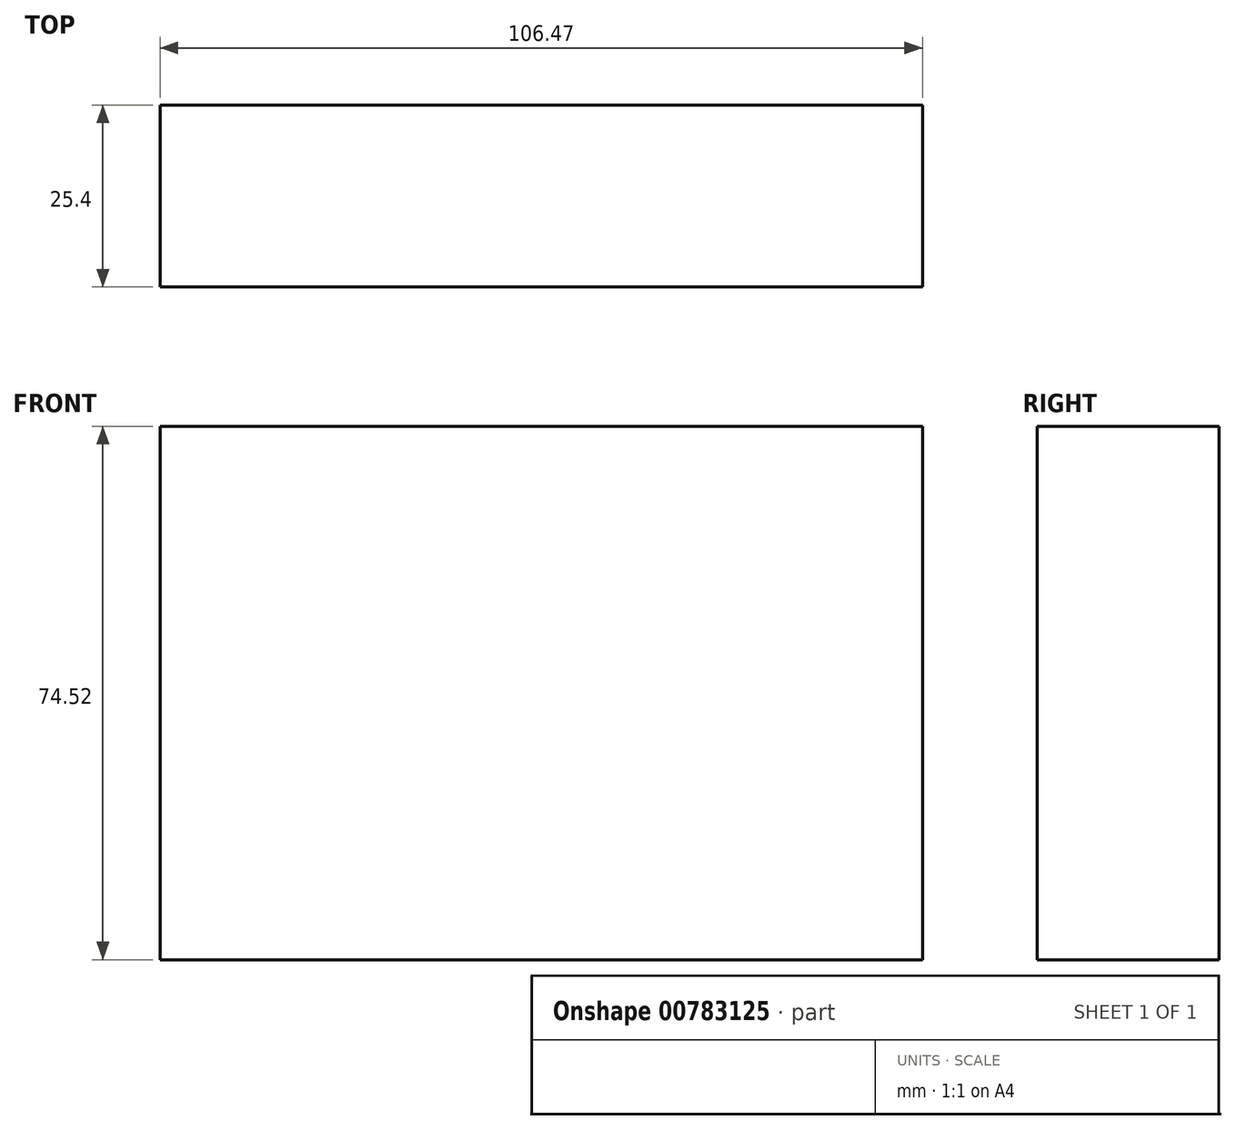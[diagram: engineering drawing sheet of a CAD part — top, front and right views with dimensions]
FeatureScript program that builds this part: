
annotation { "Feature Type Name" : "Feature", "Feature Type Description" : "" }
export const myFeature = defineFeature(function(context is Context, id is Id, definition is map)
    precondition{}
    {
        {
            var Q0;
            Q0=qCreatedBy(makeId("Front.planeOp"),FACE);
            var sketch = newSketch(context, id + "F0", { "sketchPlane" : qUnion([Q0])});
            skLineSegment(sketch, "E0.bottom", {"start": v(-50.67, 35.1) * mm, "end": v(55.8, 35.1) * mm});
            skLineSegment(sketch, "E0.top", {"start": v(-50.67, -39.43) * mm, "end": v(55.8, -39.43) * mm});
            skLineSegment(sketch, "E0.left", {"start": v(-50.67, 35.1) * mm, "end": v(-50.67, -39.43) * mm});
            skLineSegment(sketch, "E0.right", {"start": v(55.8, 35.1) * mm, "end": v(55.8, -39.43) * mm});
            skSolve(sketch);
        }
        {
            var Q0;
            Q0 = qSketchRegion(id + "F0", true);
            extrude(context, id + "F1", {"entities" : qUnion([Q0]), "depth" : 25.4 * mm, "offsetDistance" : 25.4 * mm});
        }
    });
